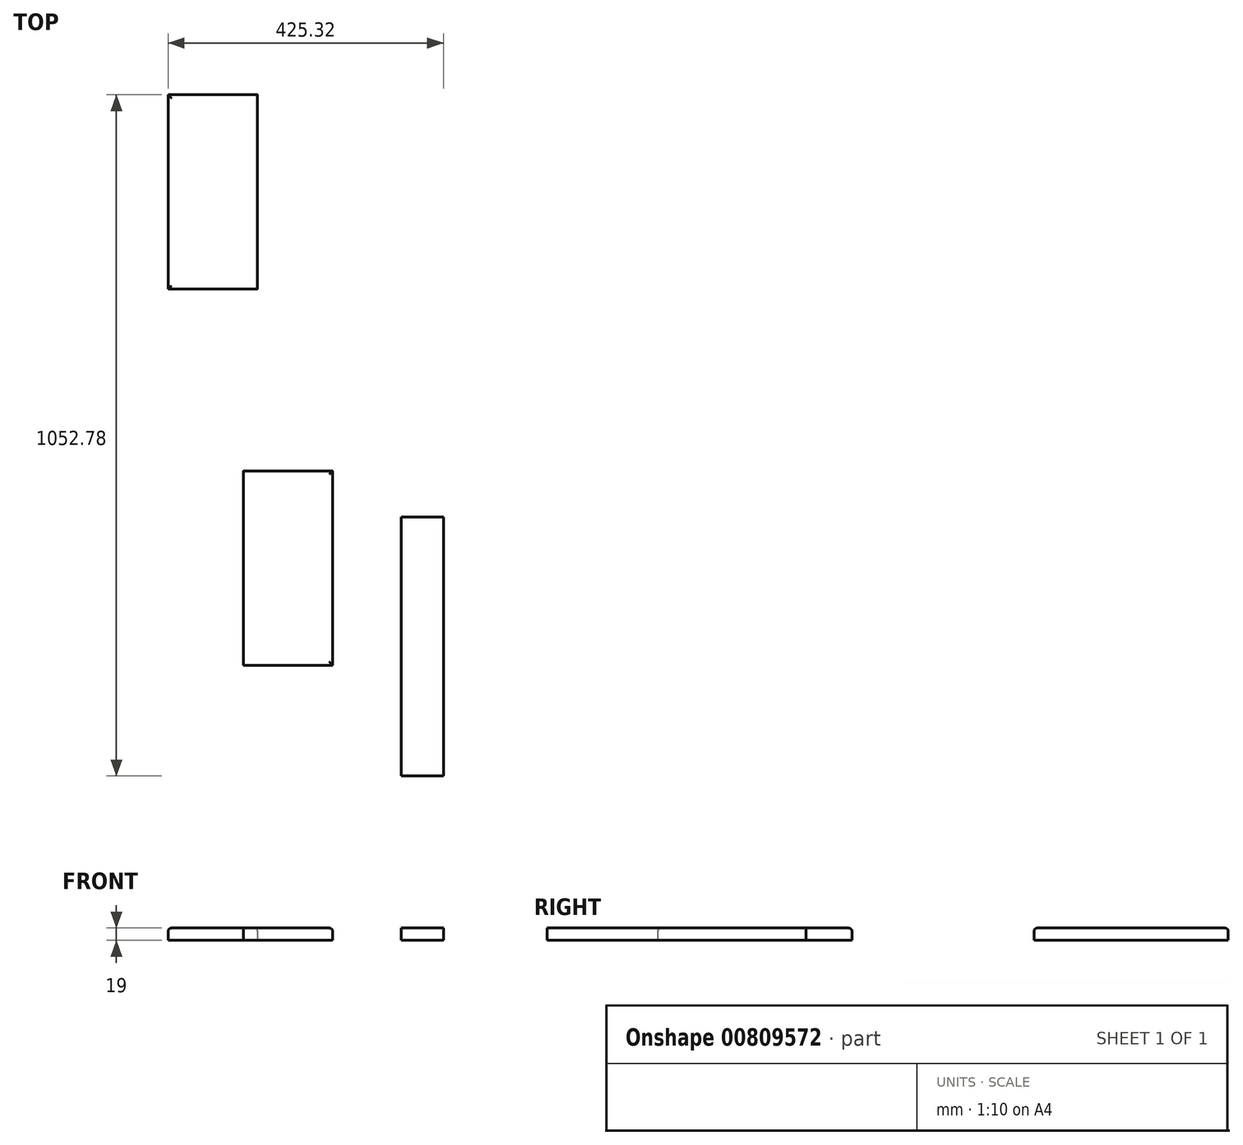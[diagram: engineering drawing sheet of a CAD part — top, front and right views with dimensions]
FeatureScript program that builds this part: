
annotation { "Feature Type Name" : "Feature", "Feature Type Description" : "" }
export const myFeature = defineFeature(function(context is Context, id is Id, definition is map)
    precondition{}
    {
        {
            var Q0;
            Q0=qCreatedBy(makeId("Top.planeOp"),FACE);
            var sketch = newSketch(context, id + "F0", { "sketchPlane" : qUnion([Q0])});
            skLineSegment(sketch, "E0.bottom", {"start": v(-179.98, 347.3) * mm, "end": v(-114.98, 347.3) * mm});
            skLineSegment(sketch, "E0.top", {"start": v(-179.98, -52.7) * mm, "end": v(-114.98, -52.7) * mm});
            skLineSegment(sketch, "E0.left", {"start": v(-179.98, 347.3) * mm, "end": v(-179.98, -52.7) * mm});
            skLineSegment(sketch, "E0.right", {"start": v(-114.98, 347.3) * mm, "end": v(-114.98, -52.7) * mm});
            skSolve(sketch);
        }
        {
            var Q0;
            Q0 = qSketchRegion(id + "F0", true);
            extrude(context, id + "F1", {"entities" : qUnion([Q0]), "depth" : 19 * mm, "offsetDistance" : 25 * mm});
        }
        {
            var Q0;
            Q0=qCreatedBy(makeId("Top.planeOp"),FACE);
            var sketch = newSketch(context, id + "F2", { "sketchPlane" : qUnion([Q0])});
            skLineSegment(sketch, "E1.bottom", {"start": v(-424.11, 418.62) * mm, "end": v(-286.11, 418.62) * mm});
            skLineSegment(sketch, "E1.top", {"start": v(-424.11, 118.62) * mm, "end": v(-286.11, 118.62) * mm});
            skLineSegment(sketch, "E1.left", {"start": v(-424.11, 418.62) * mm, "end": v(-424.11, 118.62) * mm});
            skLineSegment(sketch, "E1.right", {"start": v(-286.11, 418.62) * mm, "end": v(-286.11, 118.62) * mm});
            skSolve(sketch);
        }
        {
            var Q0;
            Q0=makeQuery(id+"F2.imprint","IMPRINT",FACE,{"disambiguationData":[TD([[makeQuery(id+"F2.imprint","IMPRINT",EDGE,{"derivedFrom":sQuery(id+"F2.wireOp",EDGE,"E1.bottom")}),-1.0]])]});
            extrude(context, id + "F3", {"entities" : qUnion([Q0]), "depth" : 19 * mm, "offsetDistance" : 25 * mm});
        }
        {
            var Q0;
            Q0=qCreatedBy(makeId("Top.planeOp"),FACE);
            var sketch = newSketch(context, id + "F4", { "sketchPlane" : qUnion([Q0])});
            skLineSegment(sketch, "E2.bottom", {"start": v(-540.3, 1000.07) * mm, "end": v(-402.3, 1000.07) * mm});
            skLineSegment(sketch, "E2.top", {"start": v(-540.3, 700.07) * mm, "end": v(-402.3, 700.07) * mm});
            skLineSegment(sketch, "E2.left", {"start": v(-540.3, 1000.07) * mm, "end": v(-540.3, 700.07) * mm});
            skLineSegment(sketch, "E2.right", {"start": v(-402.3, 1000.07) * mm, "end": v(-402.3, 700.07) * mm});
            skSolve(sketch);
        }
        {
            var Q0;
            Q0 = qSketchRegion(id + "F4", true);
            extrude(context, id + "F5", {"entities" : qUnion([Q0]), "depth" : 19 * mm, "offsetDistance" : 25 * mm});
        }
        {
            var Q0;
            Q0=makeQuery(id+"F5.opExtrude","CAP_EDGE",EDGE,{"disambiguationData":[OSD([sQuery(id+"F4.wireOp",EDGE,"E2.left")])],"isStart":false});
            var Q1;
            Q1=makeQuery(id+"F5.opExtrude","CAP_EDGE",EDGE,{"disambiguationData":[OSD([sQuery(id+"F4.wireOp",EDGE,"E2.top")])],"isStart":false});
            var Q2;
            Q2=makeQuery(id+"F5.opExtrude","CAP_EDGE",EDGE,{"disambiguationData":[OSD([sQuery(id+"F4.wireOp",EDGE,"E2.bottom")])],"isStart":false});
            var Q3;
            Q3=makeQuery(id+"F3.opExtrude","CAP_EDGE",EDGE,{"disambiguationData":[OSD([sQuery(id+"F2.wireOp",EDGE,"E1.bottom")])],"isStart":false});
            var Q4;
            Q4=makeQuery(id+"F3.opExtrude","CAP_EDGE",EDGE,{"disambiguationData":[OSD([sQuery(id+"F2.wireOp",EDGE,"E1.right")])],"isStart":false});
            var Q5;
            Q5=makeQuery(id+"F3.opExtrude","CAP_EDGE",EDGE,{"disambiguationData":[OSD([sQuery(id+"F2.wireOp",EDGE,"E1.top")])],"isStart":false});
            fillet(context, id + "F6", {"entities" : qUnion([Q0, Q1, Q2, Q3, Q4, Q5]), "radius" : 5 * mm, "tangentPropagation" : true, "allowEdgeOverflow" : false});
        }
    });
